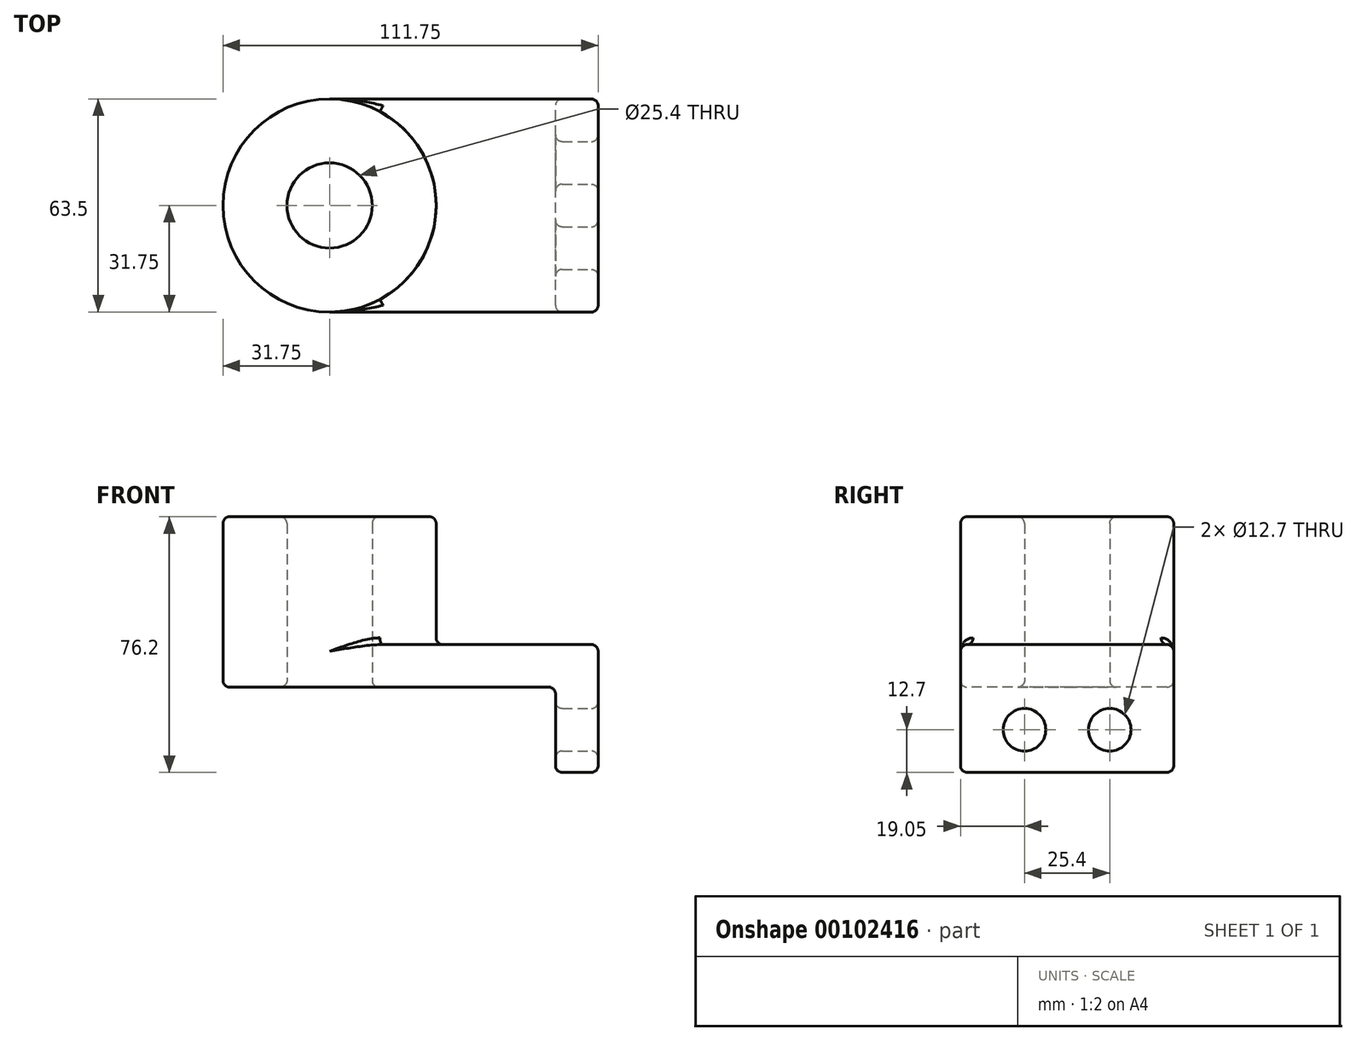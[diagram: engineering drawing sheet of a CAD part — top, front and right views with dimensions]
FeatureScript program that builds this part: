
annotation { "Feature Type Name" : "Feature", "Feature Type Description" : "" }
export const myFeature = defineFeature(function(context is Context, id is Id, definition is map)
    precondition{}
    {
        {
            var Q0;
            Q0=qCreatedBy(makeId("Top.planeOp"),FACE);
            var sketch = newSketch(context, id + "F0", { "sketchPlane" : qUnion([Q0])});
            skLineSegment(sketch, "E0.bottom", {"start": v(40, 31.75) * mm, "end": v(-40, 31.75) * mm});
            skLineSegment(sketch, "E0.top", {"start": v(40, -31.75) * mm, "end": v(-40, -31.75) * mm});
            skLineSegment(sketch, "E0.left", {"start": v(40, 31.75) * mm, "end": v(40, -31.75) * mm});
            skLineSegment(sketch, "E0.right", {"start": v(-40, 31.75) * mm, "end": v(-40, -31.75) * mm});
            skPoint(sketch, "E0.middle", {"position": v(0, 0) * mm});
            skCircle(sketch, "E1", {"center": v(-40, 0) * mm, "radius": 31.75 * mm});
            skCircle(sketch, "E2", {"center": v(-40, 0) * mm, "radius": 12.7 * mm});
            skSolve(sketch);
        }
        {
            var Q0;
            {var subQ0=sQuery(id+"F0.wireOp",EDGE,"E0.bottom");Q0=makeQuery(id+"F0.imprint","IMPRINT",FACE,{"disambiguationData":[TD([[makeQuery(id+"F0.imprint","IMPRINT",EDGE,{"derivedFrom":subQ0}),1.0]])]});}
            extrude(context, id + "F1", {"entities" : qUnion([Q0]), "depth" : 12.7 * mm});
        }
        {
            var Q0;
            {var subQ1=sQuery(id+"F0.wireOp",EDGE,"E0.right");var subQ3=sQuery(id+"F0.wireOp",EDGE,"E2");var subQ4=makeQuery(id+"F0.imprint","INTERSECT",VERTEX,{"disambiguationData":[OD(0.0)],"derivedFrom":[subQ1,subQ3]});Q0=makeQuery(id+"F0.imprint","IMPRINT",FACE,{"disambiguationData":[TD([[makeQuery(id+"F0.imprint","IMPRINT",EDGE,{"disambiguationData":[TD([[subQ4,1.0]])],"derivedFrom":subQ3}),-1.0]])]});}
            var Q1;
            {var subQ1=sQuery(id+"F0.wireOp",EDGE,"E0.right");var subQ3=sQuery(id+"F0.wireOp",EDGE,"E2");var subQ4=makeQuery(id+"F0.imprint","INTERSECT",VERTEX,{"disambiguationData":[OD(0.0)],"derivedFrom":[subQ1,subQ3]});Q1=makeQuery(id+"F0.imprint","IMPRINT",FACE,{"disambiguationData":[TD([[makeQuery(id+"F0.imprint","IMPRINT",EDGE,{"disambiguationData":[TD([[subQ4,-1.0]])],"derivedFrom":subQ3}),-1.0]])]});}
            extrude(context, id + "F2", {"entities" : qUnion([Q0, Q1]), "operationType" : NewBodyOperationType.ADD, "depth" : 50.8 * mm});
        }
        {
            var Q0;
            Q0=makeQuery(id+"F1.opExtrude","SWEPT_FACE",FACE,{"disambiguationData":[OSD([sQuery(id+"F0.wireOp",EDGE,"E0.left")])]});
            var sketch = newSketch(context, id + "F3", { "sketchPlane" : qUnion([Q0])});
            skLineSegment(sketch, "E3.bottom", {"start": v(-31.75, 12.7) * mm, "end": v(31.75, 12.7) * mm});
            skLineSegment(sketch, "E3.top", {"start": v(-31.75, -25.4) * mm, "end": v(31.75, -25.4) * mm});
            skLineSegment(sketch, "E3.left", {"start": v(-31.75, 12.7) * mm, "end": v(-31.75, -25.4) * mm});
            skLineSegment(sketch, "E3.right", {"start": v(31.75, 12.7) * mm, "end": v(31.75, -25.4) * mm});
            skCircle(sketch, "E4", {"center": v(-12.7, -12.7) * mm, "radius": 6.35 * mm});
            skLineSegment(sketch, "E5", {"start": v(0, 0) * mm, "end": v(0, -25.4) * mm});
            skCircle(sketch, "E6.MirrorC", {"center": v(12.7, -12.7) * mm, "radius": 6.35 * mm});
            skSolve(sketch);
        }
        {
            var Q0;
            Q0=makeQuery(id+"F3.imprint","IMPRINT",FACE,{"disambiguationData":[TD([[makeQuery(id+"F3.imprint","IMPRINT",EDGE,{"derivedFrom":sQuery(id+"F3.wireOp",EDGE,"E4")}),-1.0]])]});
            var Q1;
            {var subQ5=sQuery(id+"F3.wireOp",EDGE,"E5");Q1=makeQuery(id+"F3.imprint","IMPRINT",FACE,{"disambiguationData":[TD([[makeQuery(id+"F3.imprint","IMPRINT",EDGE,{"derivedFrom":subQ5}),1.0]])]});}
            extrude(context, id + "F4", {"entities" : qUnion([Q0, Q1]), "operationType" : NewBodyOperationType.ADD, "oppositeDirection" : true, "depth" : 12.7 * mm});
        }
        {
            var Q0;
            Q0=makeQuery(id+"F1.opExtrude","CAP_FACE",FACE,{"disambiguationData":[OSD([sQuery(id+"F0.wireOp",EDGE,"E0.bottom"),sQuery(id+"F0.wireOp",EDGE,"E0.top"),sQuery(id+"F0.wireOp",EDGE,"E0.left"),sQuery(id+"F0.wireOp",EDGE,"E1")])],"isStart":false});
            fillet(context, id + "F6", {"entities" : qUnion([Q0]), "radius" : 2 * mm, "tangentPropagation" : true, "allowEdgeOverflow" : false});
        }
        {
            var Q0;
            {var subQ0=sQuery(id+"F0.wireOp",EDGE,"E1");Q0=makeQuery(id+"F2.boolean.opBoolean","MERGE",FACE,{"derivedFrom":[makeQuery(id+"F1.opExtrude","CAP_FACE",FACE,{"disambiguationData":[OSD([sQuery(id+"F0.wireOp",EDGE,"E0.bottom"),sQuery(id+"F0.wireOp",EDGE,"E0.top"),sQuery(id+"F0.wireOp",EDGE,"E0.left"),subQ0])],"isStart":true}),makeQuery(id+"F2.opExtrude","CAP_FACE",FACE,{"disambiguationData":[OSD([subQ0,sQuery(id+"F0.wireOp",EDGE,"E2")])],"isStart":true})]});}
            var Q1;
            Q1=makeQuery(id+"F4.opExtrude","CAP_FACE",FACE,{"disambiguationData":[OSD([sQuery(id+"F0.wireOp",EDGE,"E0.left"),sQuery(id+"F3.wireOp",EDGE,"E3.top"),sQuery(id+"F3.wireOp",EDGE,"E3.left"),sQuery(id+"F3.wireOp",EDGE,"E3.right"),sQuery(id+"F3.wireOp",EDGE,"E4"),sQuery(id+"F3.wireOp",EDGE,"E6.MirrorC")])],"isStart":false});
            var Q2;
            Q2=makeQuery(id+"F4.opExtrude","SWEPT_FACE",FACE,{"disambiguationData":[OSD([sQuery(id+"F3.wireOp",EDGE,"E3.top")])]});
            fillet(context, id + "F7", {"entities" : qUnion([Q0, Q1, Q2]), "radius" : 2 * mm, "tangentPropagation" : true, "allowEdgeOverflow" : false});
        }
        {
            var Q0;
            Q0=makeQuery(id+"F4.boolean.opBoolean","MERGE",EDGE,{"derivedFrom":[makeQuery(id+"F1.opExtrude","SWEPT_EDGE",EDGE,{"disambiguationData":[OSD([sQuery(id+"F0.wireOp",EDGE,"E0.top"),sQuery(id+"F0.wireOp",EDGE,"E0.left")])]}),makeQuery(id+"F4.opExtrude","CAP_EDGE",EDGE,{"disambiguationData":[OSD([sQuery(id+"F3.wireOp",EDGE,"E3.left")])],"isStart":true})]});
            var Q1;
            Q1=makeQuery(id+"F4.boolean.opBoolean","MERGE",EDGE,{"derivedFrom":[makeQuery(id+"F1.opExtrude","SWEPT_EDGE",EDGE,{"disambiguationData":[OSD([sQuery(id+"F0.wireOp",EDGE,"E0.bottom"),sQuery(id+"F0.wireOp",EDGE,"E0.left")])]}),makeQuery(id+"F4.opExtrude","CAP_EDGE",EDGE,{"disambiguationData":[OSD([sQuery(id+"F3.wireOp",EDGE,"E3.right")])],"isStart":true})]});
            var Q2;
            Q2=makeQuery(id+"F4.opExtrude","CAP_EDGE",EDGE,{"disambiguationData":[OSD([sQuery(id+"F3.wireOp",EDGE,"E6.MirrorC")])],"isStart":true});
            var Q3;
            Q3=makeQuery(id+"F4.opExtrude","CAP_EDGE",EDGE,{"disambiguationData":[OSD([sQuery(id+"F3.wireOp",EDGE,"E4")])],"isStart":true});
            fillet(context, id + "F5", {"entities" : qUnion([Q0, Q1, Q2, Q3]), "radius" : 2 * mm, "tangentPropagation" : true, "allowEdgeOverflow" : false});
        }
        {
            var Q0;
            Q0=makeQuery(id+"F2.opExtrude","CAP_FACE",FACE,{"disambiguationData":[OSD([sQuery(id+"F0.wireOp",EDGE,"E1"),sQuery(id+"F0.wireOp",EDGE,"E2")])],"isStart":false});
            fillet(context, id + "F8", {"entities" : qUnion([Q0]), "radius" : 2 * mm, "tangentPropagation" : true, "allowEdgeOverflow" : false});
        }
    });
